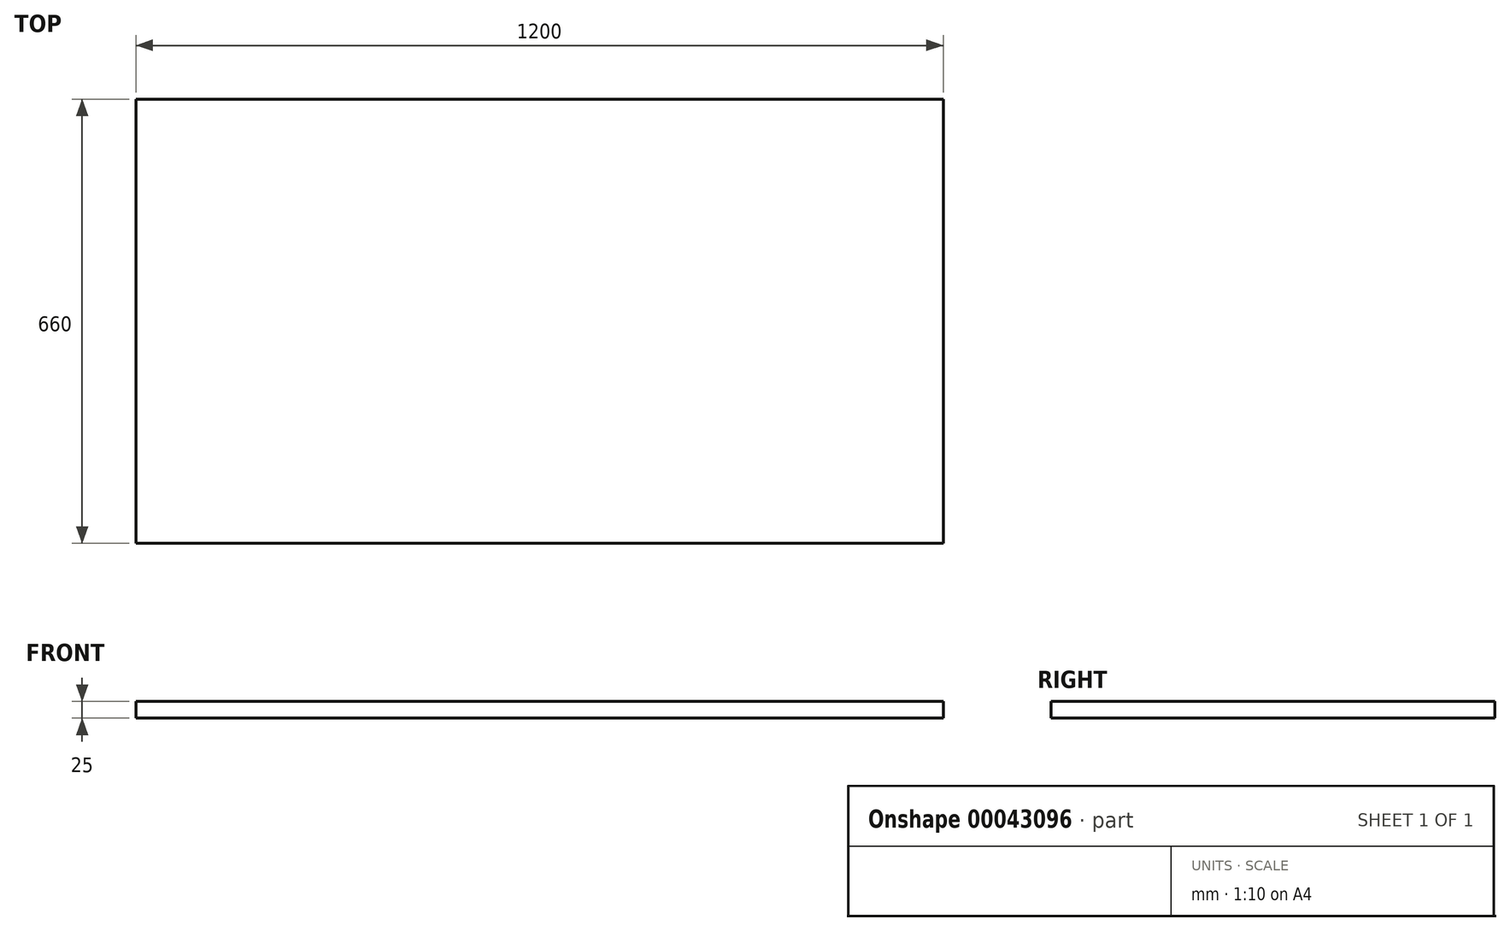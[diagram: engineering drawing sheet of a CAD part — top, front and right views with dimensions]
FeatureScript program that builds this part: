
annotation { "Feature Type Name" : "Feature", "Feature Type Description" : "" }
export const myFeature = defineFeature(function(context is Context, id is Id, definition is map)
    precondition{}
    {
        {
            var Q0;
            Q0=qCreatedBy(makeId("Top.planeOp"),FACE);
            var sketch = newSketch(context, id + "F0", { "sketchPlane" : qUnion([Q0])});
            skLineSegment(sketch, "E0.bottom", {"start": v(0, 0) * mm, "end": v(1200, 0) * mm});
            skLineSegment(sketch, "E0.top", {"start": v(0, -660) * mm, "end": v(1200, -660) * mm});
            skLineSegment(sketch, "E0.left", {"start": v(0, 0) * mm, "end": v(0, -660) * mm});
            skLineSegment(sketch, "E0.right", {"start": v(1200, 0) * mm, "end": v(1200, -660) * mm});
            skSolve(sketch);
        }
        {
            var Q0;
            Q0=makeQuery(id+"F0.imprint","IMPRINT",FACE,{"disambiguationData":[TD([[makeQuery(id+"F0.imprint","IMPRINT",EDGE,{"derivedFrom":sQuery(id+"F0.wireOp",EDGE,"E0.bottom")}),-1.0]])]});
            extrude(context, id + "F1", {"entities" : qUnion([Q0]), "depth" : 25 * mm});
        }
    });
